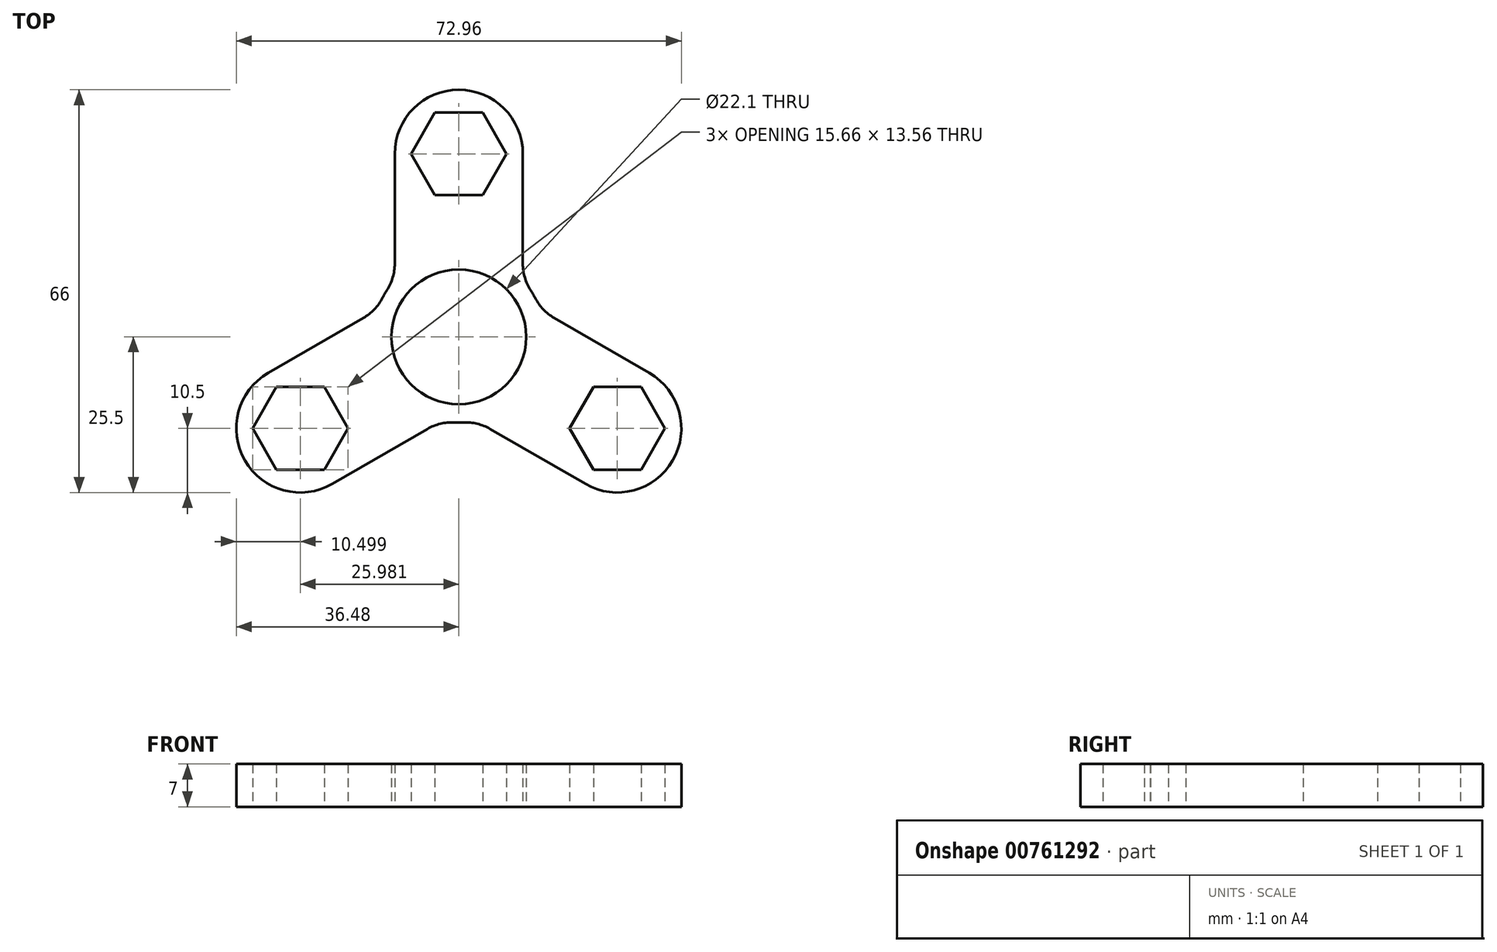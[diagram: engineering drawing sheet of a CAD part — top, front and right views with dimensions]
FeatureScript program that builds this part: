
annotation { "Feature Type Name" : "Feature", "Feature Type Description" : "" }
export const myFeature = defineFeature(function(context is Context, id is Id, definition is map)
    precondition{}
    {
        {
            var Q0;
            Q0=qCreatedBy(makeId("Top.planeOp"),FACE);
            var sketch = newSketch(context, id + "F0", { "sketchPlane" : qUnion([Q0])});
            skCircle(sketch, "E0", {"center": v(0, 0) * mm, "radius": 11.05 * mm});
            skCircle(sketch, "E1.0", {"center": v(0, 0) * mm, "radius": 14.05 * mm});
            skCircle(sketch, "E2.cCircle", {"center": v(0, 30) * mm, "radius": 7.83 * mm, "construction": true});
            skLineSegment(sketch, "E2.0", {"start": v(3.91, 23.22) * mm, "end": v(-3.91, 23.22) * mm});
            skLineSegment(sketch, "E2.1", {"start": v(-3.91, 23.22) * mm, "end": v(-7.83, 30) * mm});
            skLineSegment(sketch, "E2.2", {"start": v(-7.83, 30) * mm, "end": v(-3.91, 36.78) * mm});
            skLineSegment(sketch, "E2.3", {"start": v(-3.91, 36.78) * mm, "end": v(3.91, 36.78) * mm});
            skLineSegment(sketch, "E2.4", {"start": v(3.91, 36.78) * mm, "end": v(7.83, 30) * mm});
            skLineSegment(sketch, "E2.5", {"start": v(7.83, 30) * mm, "end": v(3.91, 23.22) * mm});
            skCircle(sketch, "E3", {"center": v(0, 30) * mm, "radius": 10.5 * mm});
            skPoint(sketch, "E4.center", {"position": v(0, 0.24) * mm});
            skLineSegment(sketch, "E5", {"start": v(10.5, 30) * mm, "end": v(10.5, 9.34) * mm});
            skLineSegment(sketch, "E6", {"start": v(-10.5, 30) * mm, "end": v(-10.5, 9.34) * mm});
            skCircle(sketch, "E7.1.0", {"center": v(-25.98, -15) * mm, "radius": 7.83 * mm, "construction": true});
            skLineSegment(sketch, "E7.1.1", {"start": v(-22.07, -8.22) * mm, "end": v(-18.15, -15) * mm});
            skLineSegment(sketch, "E7.1.2", {"start": v(-31.23, -5.9) * mm, "end": v(-13.33, 4.43) * mm});
            skLineSegment(sketch, "E7.1.3", {"start": v(-29.9, -8.22) * mm, "end": v(-22.07, -8.22) * mm});
            skLineSegment(sketch, "E7.1.4", {"start": v(-20.73, -24.1) * mm, "end": v(-2.83, -13.76) * mm});
            skLineSegment(sketch, "E7.1.5", {"start": v(-29.9, -21.78) * mm, "end": v(-33.8, -15) * mm});
            skCircle(sketch, "E7.1.6", {"center": v(-25.98, -15) * mm, "radius": 10.5 * mm});
            skLineSegment(sketch, "E7.1.7", {"start": v(-18.15, -15) * mm, "end": v(-22.07, -21.78) * mm});
            skLineSegment(sketch, "E7.1.8", {"start": v(-33.8, -15) * mm, "end": v(-29.9, -8.22) * mm});
            skLineSegment(sketch, "E7.1.9", {"start": v(-22.07, -21.78) * mm, "end": v(-29.9, -21.78) * mm});
            skCircle(sketch, "E7.2.0", {"center": v(25.98, -15) * mm, "radius": 7.83 * mm, "construction": true});
            skLineSegment(sketch, "E7.2.1", {"start": v(18.15, -15) * mm, "end": v(22.07, -8.22) * mm});
            skLineSegment(sketch, "E7.2.2", {"start": v(20.73, -24.1) * mm, "end": v(2.83, -13.76) * mm});
            skLineSegment(sketch, "E7.2.3", {"start": v(22.07, -21.78) * mm, "end": v(18.15, -15) * mm});
            skLineSegment(sketch, "E7.2.4", {"start": v(31.23, -5.9) * mm, "end": v(13.33, 4.43) * mm});
            skLineSegment(sketch, "E7.2.5", {"start": v(33.8, -15) * mm, "end": v(29.9, -21.78) * mm});
            skCircle(sketch, "E7.2.6", {"center": v(25.98, -15) * mm, "radius": 10.5 * mm});
            skLineSegment(sketch, "E7.2.7", {"start": v(22.07, -8.22) * mm, "end": v(29.9, -8.22) * mm});
            skLineSegment(sketch, "E7.2.8", {"start": v(29.9, -21.78) * mm, "end": v(22.07, -21.78) * mm});
            skLineSegment(sketch, "E7.2.9", {"start": v(29.9, -8.22) * mm, "end": v(33.8, -15) * mm});
            skSolve(sketch);
        }
        {
            var Q0;
            Q0=makeQuery(id+"F0.imprint","IMPRINT",FACE,{"disambiguationData":[TD([[makeQuery(id+"F0.imprint","IMPRINT",EDGE,{"derivedFrom":sQuery(id+"F0.wireOp",EDGE,"E2.0")}),1.0]])]});
            var Q1;
            {var subQ0=sQuery(id+"F0.wireOp",EDGE,"E5");Q1=makeQuery(id+"F0.imprint","IMPRINT",FACE,{"disambiguationData":[TD([[makeQuery(id+"F0.imprint","IMPRINT",EDGE,{"derivedFrom":subQ0}),-1.0]])]});}
            var Q2;
            Q2=makeQuery(id+"F0.imprint","IMPRINT",FACE,{"disambiguationData":[TD([[makeQuery(id+"F0.imprint","IMPRINT",EDGE,{"derivedFrom":sQuery(id+"F0.wireOp",EDGE,"E0")}),-1.0]])]});
            var Q3;
            {var subQ0=sQuery(id+"F0.wireOp",EDGE,"E7.1.2");Q3=makeQuery(id+"F0.imprint","IMPRINT",FACE,{"disambiguationData":[TD([[makeQuery(id+"F0.imprint","IMPRINT",EDGE,{"derivedFrom":subQ0}),-1.0]])]});}
            var Q4;
            Q4=makeQuery(id+"F0.imprint","IMPRINT",FACE,{"disambiguationData":[TD([[makeQuery(id+"F0.imprint","IMPRINT",EDGE,{"derivedFrom":sQuery(id+"F0.wireOp",EDGE,"E7.1.1")}),1.0]])]});
            var Q5;
            {var subQ0=sQuery(id+"F0.wireOp",EDGE,"E7.2.2");Q5=makeQuery(id+"F0.imprint","IMPRINT",FACE,{"disambiguationData":[TD([[makeQuery(id+"F0.imprint","IMPRINT",EDGE,{"derivedFrom":subQ0}),-1.0]])]});}
            var Q6;
            Q6=makeQuery(id+"F0.imprint","IMPRINT",FACE,{"disambiguationData":[TD([[makeQuery(id+"F0.imprint","IMPRINT",EDGE,{"derivedFrom":sQuery(id+"F0.wireOp",EDGE,"E7.2.1")}),1.0]])]});
            extrude(context, id + "F1", {"entities" : qUnion([Q0, Q1, Q2, Q3, Q4, Q5, Q6]), "depth" : 7 * mm, "offsetDistance" : 25 * mm});
        }
        {
            var Q0;
            Q0=makeQuery(id+"F1.opExtrude","SWEPT_EDGE",EDGE,{"disambiguationData":[OSD([sQuery(id+"F0.wireOp",EDGE,"E1.0"),sQuery(id+"F0.wireOp",EDGE,"E6")])]});
            var Q1;
            Q1=makeQuery(id+"F1.opExtrude","SWEPT_EDGE",EDGE,{"disambiguationData":[OSD([sQuery(id+"F0.wireOp",EDGE,"E1.0"),sQuery(id+"F0.wireOp",EDGE,"E7.1.2")])]});
            var Q2;
            Q2=makeQuery(id+"F1.opExtrude","SWEPT_EDGE",EDGE,{"disambiguationData":[OSD([sQuery(id+"F0.wireOp",EDGE,"E1.0"),sQuery(id+"F0.wireOp",EDGE,"E5")])]});
            var Q3;
            Q3=makeQuery(id+"F1.opExtrude","SWEPT_EDGE",EDGE,{"disambiguationData":[OSD([sQuery(id+"F0.wireOp",EDGE,"E1.0"),sQuery(id+"F0.wireOp",EDGE,"E7.2.4")])]});
            var Q4;
            Q4=makeQuery(id+"F1.opExtrude","SWEPT_EDGE",EDGE,{"disambiguationData":[OSD([sQuery(id+"F0.wireOp",EDGE,"E1.0"),sQuery(id+"F0.wireOp",EDGE,"E7.1.4")])]});
            var Q5;
            Q5=makeQuery(id+"F1.opExtrude","SWEPT_EDGE",EDGE,{"disambiguationData":[OSD([sQuery(id+"F0.wireOp",EDGE,"E1.0"),sQuery(id+"F0.wireOp",EDGE,"E7.2.2")])]});
            fillet(context, id + "F2", {"entities" : qUnion([Q0, Q1, Q2, Q3, Q4, Q5]), "radius" : 8 * mm, "tangentPropagation" : true, "allowEdgeOverflow" : false});
        }
    });
